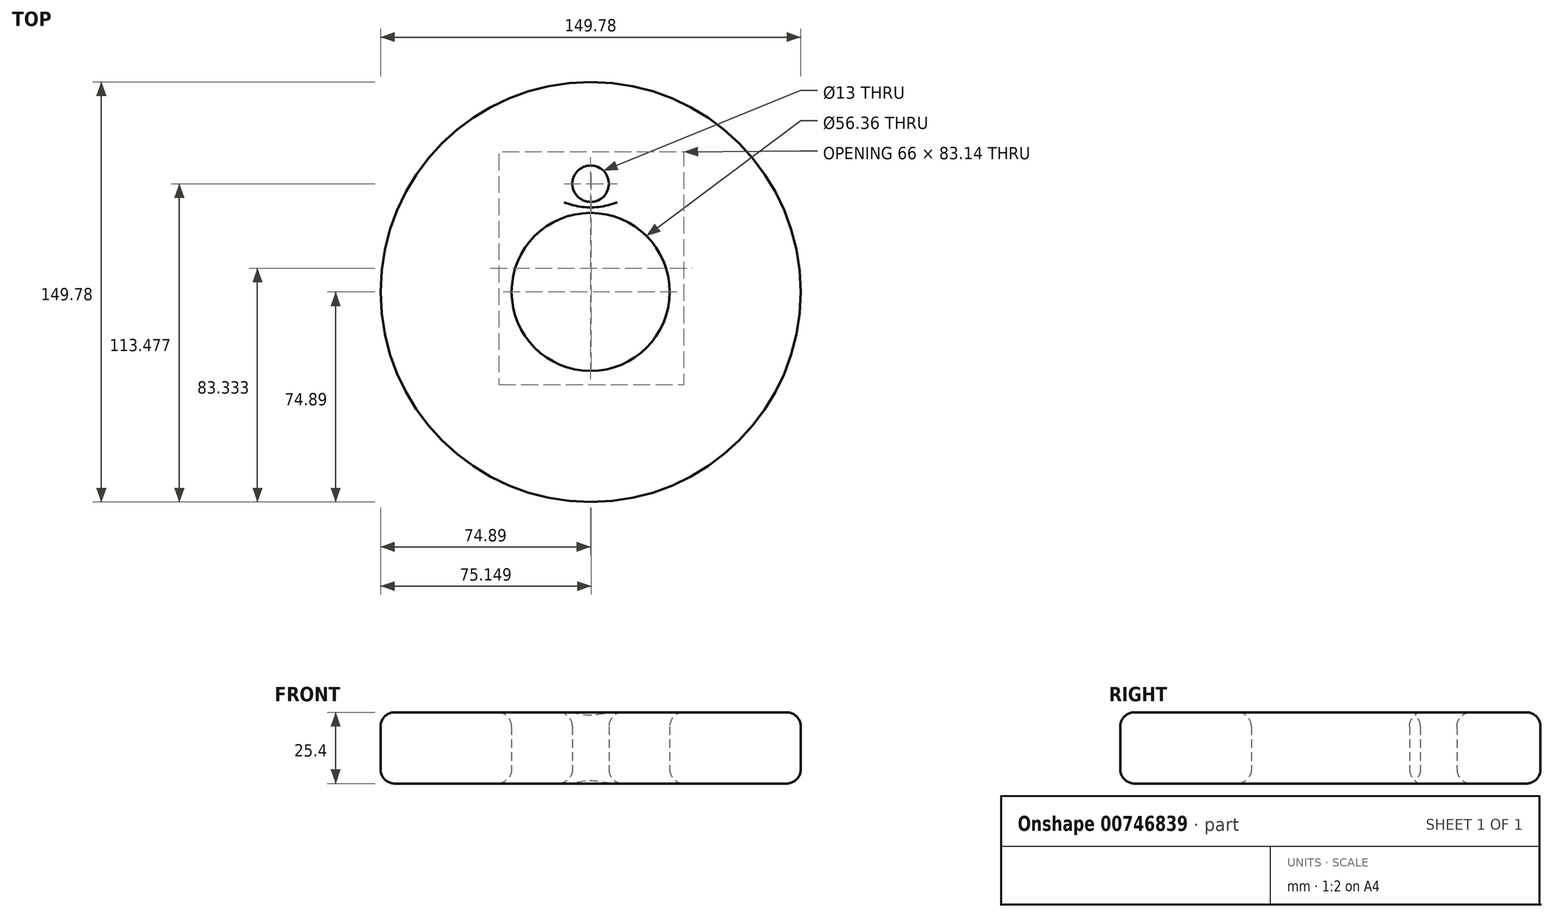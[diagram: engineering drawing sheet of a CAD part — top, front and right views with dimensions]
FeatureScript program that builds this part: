
annotation { "Feature Type Name" : "Feature", "Feature Type Description" : "" }
export const myFeature = defineFeature(function(context is Context, id is Id, definition is map)
    precondition{}
    {
        {
            var Q0;
            Q0=qCreatedBy(makeId("Top.planeOp"),FACE);
            var sketch = newSketch(context, id + "F0", { "sketchPlane" : qUnion([Q0])});
            skCircle(sketch, "E0", {"center": v(0, 0) * mm, "radius": 74.9 * mm});
            skCircle(sketch, "E1", {"center": v(0, 38.59) * mm, "radius": 6.5 * mm});
            skCircle(sketch, "E2", {"center": v(0, 0) * mm, "radius": 28.18 * mm});
            skSolve(sketch);
        }
        {
            var Q0;
            Q0=makeQuery(id+"F0.imprint","IMPRINT",FACE,{"disambiguationData":[TD([[makeQuery(id+"F0.imprint","IMPRINT",EDGE,{"derivedFrom":sQuery(id+"F0.wireOp",EDGE,"E0")}),1.0]])]});
            extrude(context, id + "F1", {"entities" : qUnion([Q0]), "depth" : 25.4 * mm, "offsetDistance" : 25.4 * mm});
        }
        {
            var Q0;
            Q0=makeQuery(id+"F1.opExtrude","CAP_FACE",FACE,{"disambiguationData":[OSD([sQuery(id+"F0.wireOp",EDGE,"E0"),sQuery(id+"F0.wireOp",EDGE,"E1"),sQuery(id+"F0.wireOp",EDGE,"E2")])],"isStart":false});
            var Q1;
            Q1=makeQuery(id+"F1.opExtrude","CAP_EDGE",EDGE,{"disambiguationData":[OSD([sQuery(id+"F0.wireOp",EDGE,"E0")])],"isStart":false});
            var Q2;
            Q2=makeQuery(id+"F1.opExtrude","CAP_EDGE",EDGE,{"disambiguationData":[OSD([sQuery(id+"F0.wireOp",EDGE,"E1")])],"isStart":true});
            var Q3;
            Q3=makeQuery(id+"F1.opExtrude","CAP_EDGE",EDGE,{"disambiguationData":[OSD([sQuery(id+"F0.wireOp",EDGE,"E2")])],"isStart":true});
            var Q4;
            Q4=makeQuery(id+"F1.opExtrude","SWEPT_FACE",FACE,{"disambiguationData":[OSD([sQuery(id+"F0.wireOp",EDGE,"E0")])]});
            var Q5;
            Q5=makeQuery(id+"F1.opExtrude","CAP_EDGE",EDGE,{"disambiguationData":[OSD([sQuery(id+"F0.wireOp",EDGE,"E0")])],"isStart":true});
            fillet(context, id + "F2", {"entities" : qUnion([Q0, Q1, Q2, Q3, Q4, Q5]), "radius" : 5.08 * mm, "tangentPropagation" : true, "allowEdgeOverflow" : false});
        }
    });
